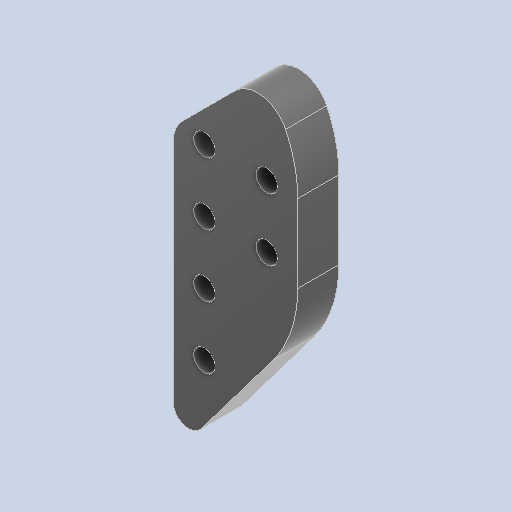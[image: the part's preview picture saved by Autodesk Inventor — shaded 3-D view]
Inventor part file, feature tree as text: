
AUTODESK INVENTOR PART (.ipt)
format: ipt  version: 2023 (Build 270158000, 158)  size: 126,464 bytes
history: native  units: in
note: dims shown in document units (in); Inventor stores cm internally (conversion verified against a paired STEP export)
features: other x3, sketch x1, plane x1
ambient origin geometry x8: Origin, YZ Plane, XZ Plane, XY Plane, X Axis, Y Axis, Z Axis, Center Point
bodies: Solid1 (feature_tree)
feature tree (5):
  other  "IntakeArmSpacingBlock.ipt"
  other  "Solid1::IntakeArmSpacingBlock.ipt"
  other  "TaggingFeature1"
  sketch  "Sketch1"  dims[d0=0.3937in]
  plane  "Work Plane1"
